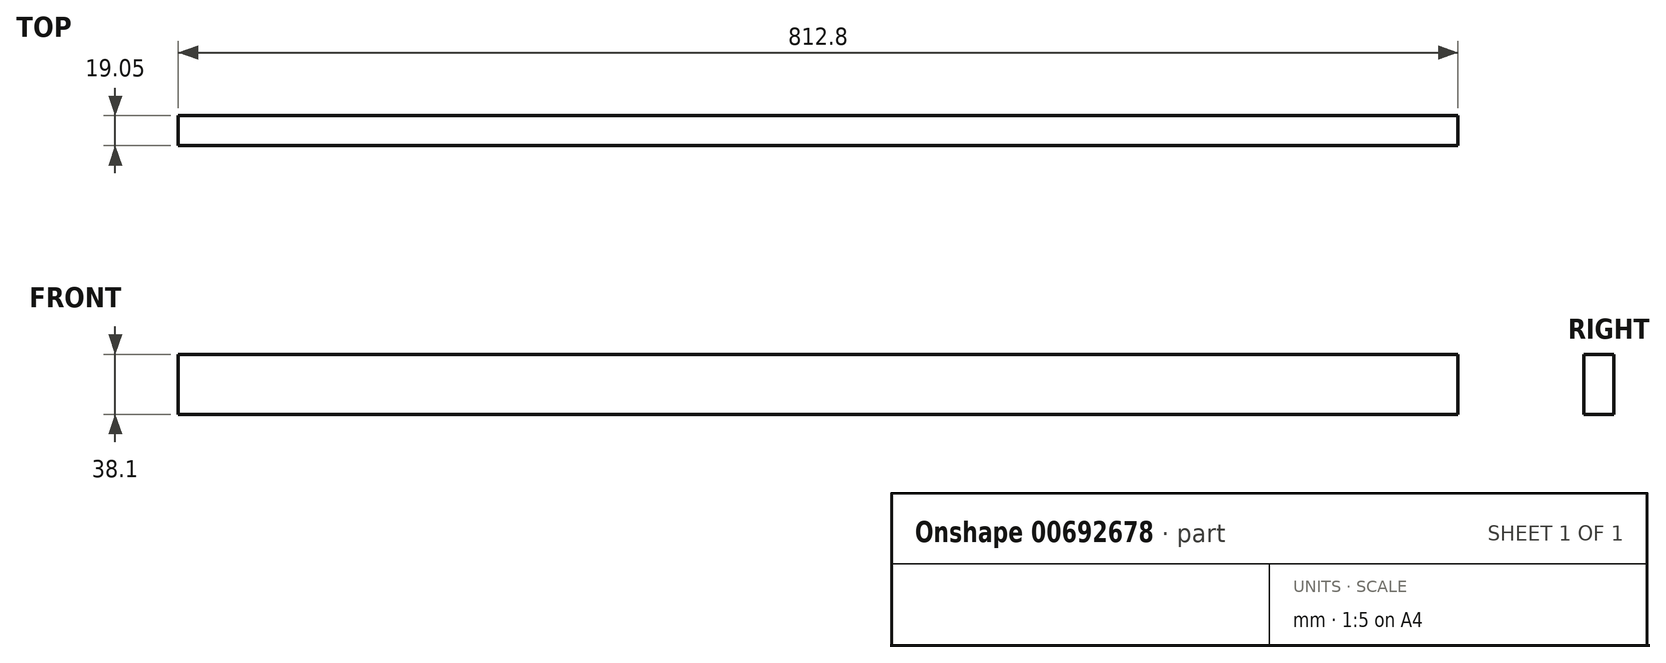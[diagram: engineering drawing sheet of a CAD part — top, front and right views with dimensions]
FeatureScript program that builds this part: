
annotation { "Feature Type Name" : "Feature", "Feature Type Description" : "" }
export const myFeature = defineFeature(function(context is Context, id is Id, definition is map)
    precondition{}
    {
        {
            var Q0;
            Q0=qCreatedBy(makeId("Front.planeOp"),FACE);
            var sketch = newSketch(context, id + "F0", { "sketchPlane" : qUnion([Q0])});
            skLineSegment(sketch, "E0.bottom", {"start": v(734.36, 18.04) * mm, "end": v(-78.44, 18.04) * mm});
            skLineSegment(sketch, "E0.top", {"start": v(734.36, -13.7) * mm, "end": v(-78.44, -13.7) * mm});
            skLineSegment(sketch, "E0.left", {"start": v(734.36, 18.04) * mm, "end": v(734.36, -13.7) * mm});
            skLineSegment(sketch, "E0.right", {"start": v(-78.44, 18.04) * mm, "end": v(-78.44, -13.7) * mm});
            skSolve(sketch);
        }
        {
            var Q0;
            Q0=makeQuery(id+"F0.imprint","IMPRINT",FACE,{"disambiguationData":[TD([[makeQuery(id+"F0.imprint","IMPRINT",EDGE,{"derivedFrom":sQuery(id+"F0.wireOp",EDGE,"E0.bottom")}),1.0]])]});
            extrude(context, id + "F1", {"entities" : qUnion([Q0]), "depth" : 19.05 * mm, "offsetDistance" : 25.4 * mm});
        }
        {
            var Q0;
            Q0=makeQuery(id+"F1.opExtrude","SWEPT_FACE",FACE,{"disambiguationData":[OSD([sQuery(id+"F0.wireOp",EDGE,"E0.top")])]});
            extrude(context, id + "F2", {"entities" : qUnion([Q0]), "operationType" : NewBodyOperationType.ADD, "depth" : 6.35 * mm, "offsetDistance" : 25.4 * mm});
        }
    });
